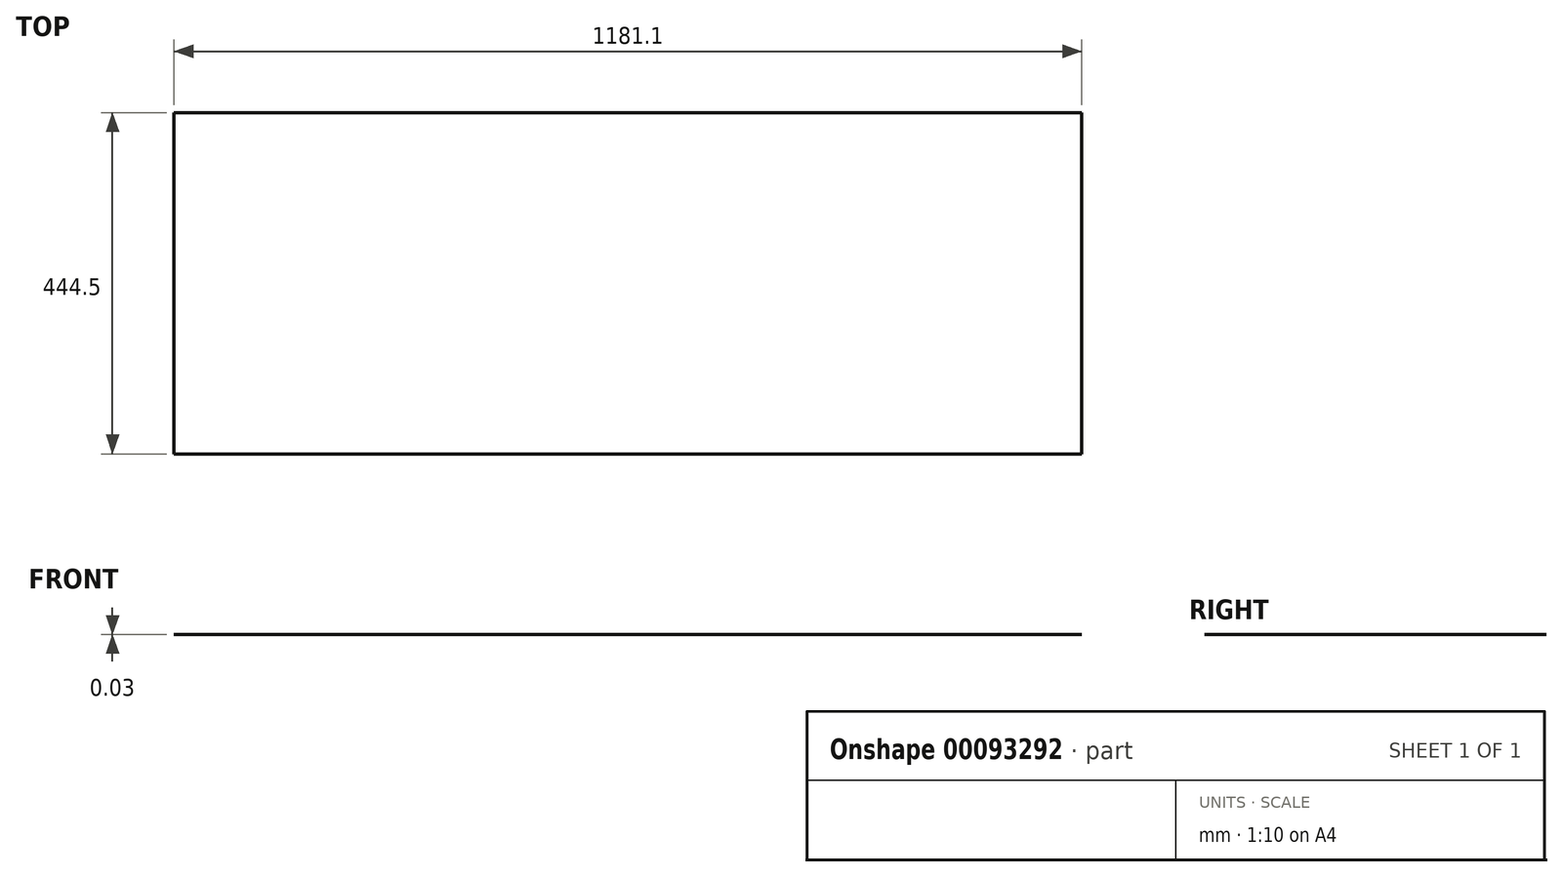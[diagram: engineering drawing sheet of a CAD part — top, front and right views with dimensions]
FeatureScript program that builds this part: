
annotation { "Feature Type Name" : "Feature", "Feature Type Description" : "" }
export const myFeature = defineFeature(function(context is Context, id is Id, definition is map)
    precondition{}
    {
        {
            var Q0;
            Q0=qCreatedBy(makeId("Top.planeOp"),FACE);
            var sketch = newSketch(context, id + "F0", { "sketchPlane" : qUnion([Q0])});
            skLineSegment(sketch, "E0.bottom", {"start": v(-590.55, 0) * mm, "end": v(590.55, 0) * mm});
            skLineSegment(sketch, "E0.top", {"start": v(-590.55, 444.5) * mm, "end": v(590.55, 444.5) * mm});
            skLineSegment(sketch, "E0.left", {"start": v(-590.55, 0) * mm, "end": v(-590.55, 444.5) * mm});
            skLineSegment(sketch, "E0.right", {"start": v(590.55, 0) * mm, "end": v(590.55, 444.5) * mm});
            skSolve(sketch);
        }
        {
            var Q0;
            Q0=makeQuery(id+"F0.imprint","IMPRINT",FACE,{"disambiguationData":[TD([[makeQuery(id+"F0.imprint","IMPRINT",EDGE,{"derivedFrom":sQuery(id+"F0.wireOp",EDGE,"E0.bottom")}),1.0]])]});
            extrude(context, id + "F1", {"entities" : qUnion([Q0]), "depth" : 3 / 101.6 * mm});
        }
    });
